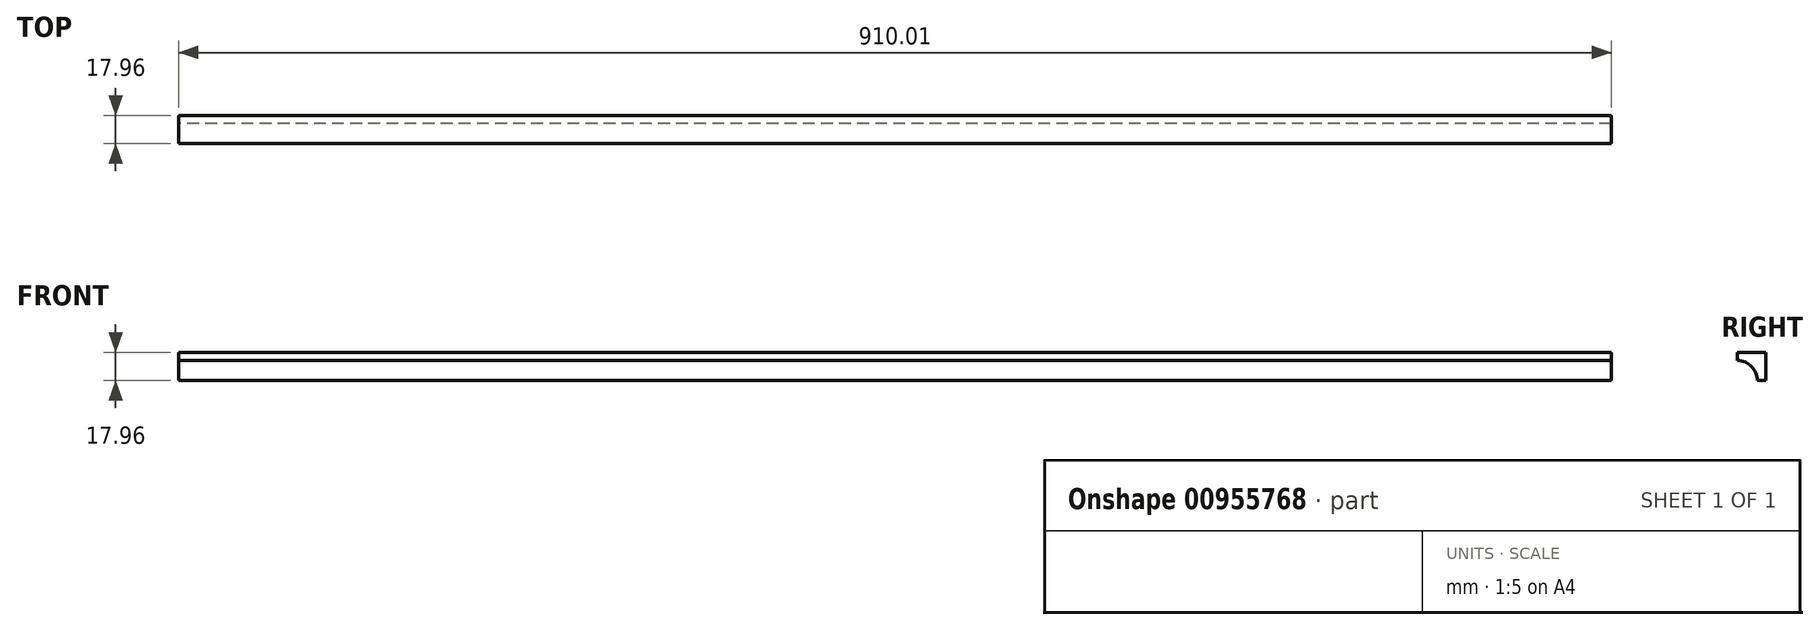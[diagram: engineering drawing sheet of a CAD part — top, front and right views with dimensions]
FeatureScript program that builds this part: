
annotation { "Feature Type Name" : "Feature", "Feature Type Description" : "" }
export const myFeature = defineFeature(function(context is Context, id is Id, definition is map)
    precondition{}
    {
        {
            var Q0;
            Q0=qCreatedBy(makeId("Right.planeOp"),FACE);
            var sketch = newSketch(context, id + "F0", { "sketchPlane" : qUnion([Q0])});
            skLineSegment(sketch, "E0.bottom", {"start": v(-21.76, 28.2) * mm, "end": v(-39.72, 28.2) * mm});
            skLineSegment(sketch, "E0.top", {"start": v(-21.76, 46.16) * mm, "end": v(-39.72, 46.16) * mm});
            skLineSegment(sketch, "E0.left", {"start": v(-21.76, 28.2) * mm, "end": v(-21.76, 46.16) * mm});
            skLineSegment(sketch, "E0.right", {"start": v(-39.72, 28.2) * mm, "end": v(-39.72, 46.16) * mm});
            skPoint(sketch, "E0.middle", {"position": v(-30.74, 37.18) * mm});
            skCircle(sketch, "E1", {"center": v(-39.72, 28.2) * mm, "radius": 12.7 * mm});
            skSolve(sketch);
        }
        {
            var Q0;
            {var subQ1=sQuery(id+"F0.wireOp",EDGE,"E0.top");Q0=makeQuery(id+"F0.imprint","IMPRINT",FACE,{"disambiguationData":[TD([[makeQuery(id+"F0.imprint","IMPRINT",EDGE,{"derivedFrom":subQ1}),1.0]])]});}
            extrude(context, id + "F1", {"entities" : qUnion([Q0]), "depth" : 910 * mm, "offsetDistance" : 25.4 * mm});
        }
    });
